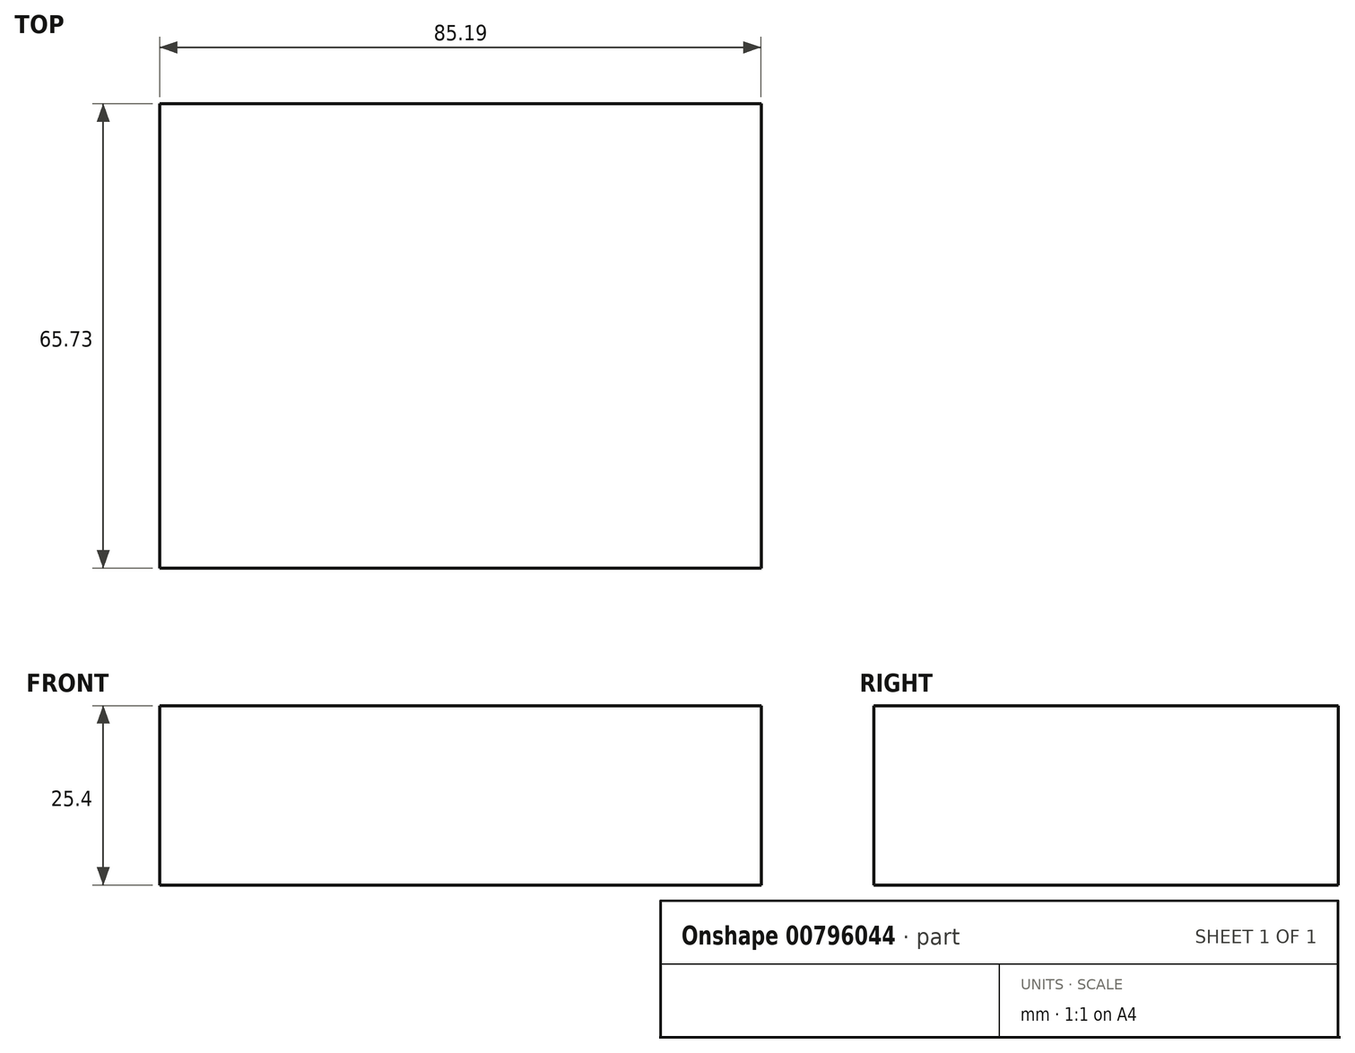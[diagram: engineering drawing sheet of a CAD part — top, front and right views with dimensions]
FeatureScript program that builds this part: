
annotation { "Feature Type Name" : "Feature", "Feature Type Description" : "" }
export const myFeature = defineFeature(function(context is Context, id is Id, definition is map)
    precondition{}
    {
        {
            var Q0;
            Q0=qCreatedBy(makeId("Top.planeOp"),FACE);
            var sketch = newSketch(context, id + "F0", { "sketchPlane" : qUnion([Q0])});
            skLineSegment(sketch, "E0.bottom", {"start": v(-47.28, 48.79) * mm, "end": v(37.91, 48.79) * mm});
            skLineSegment(sketch, "E0.top", {"start": v(-47.28, -16.94) * mm, "end": v(37.91, -16.94) * mm});
            skLineSegment(sketch, "E0.left", {"start": v(-47.28, 48.79) * mm, "end": v(-47.28, -16.94) * mm});
            skLineSegment(sketch, "E0.right", {"start": v(37.91, 48.79) * mm, "end": v(37.91, -16.94) * mm});
            skSolve(sketch);
        }
        {
            var Q0;
            Q0 = qSketchRegion(id + "F0", true);
            extrude(context, id + "F1", {"entities" : qUnion([Q0]), "depth" : 25.4 * mm, "offsetDistance" : 25.4 * mm});
        }
    });
